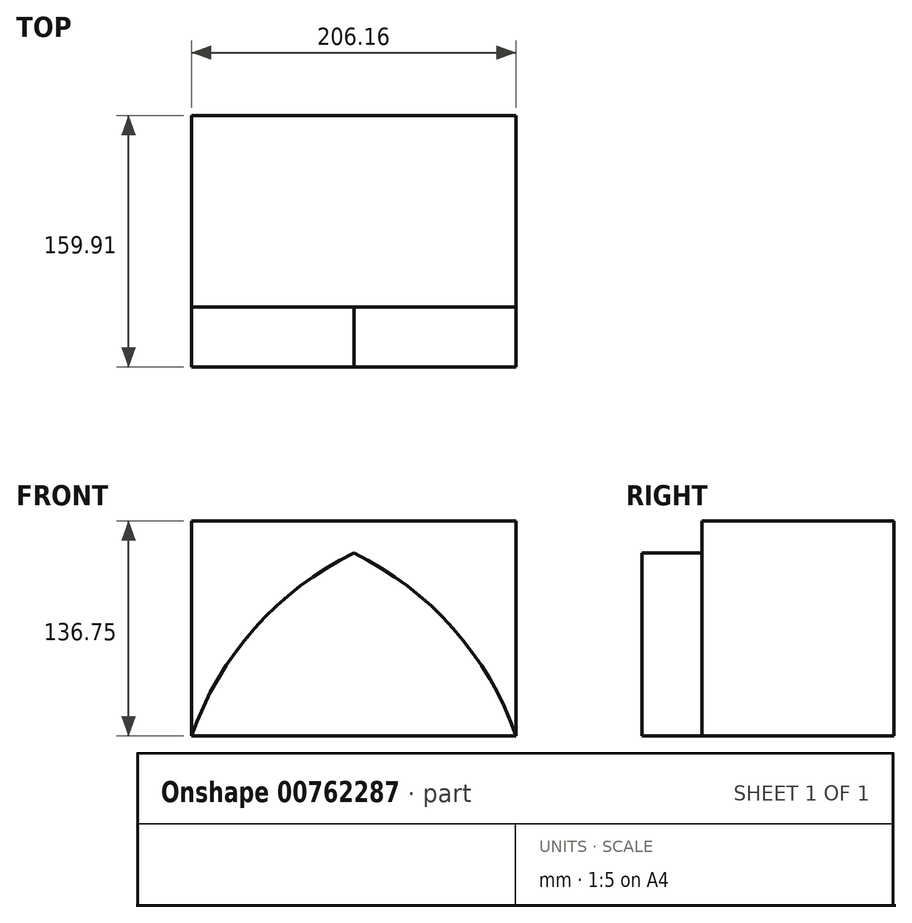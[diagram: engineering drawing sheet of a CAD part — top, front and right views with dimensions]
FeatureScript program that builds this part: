
annotation { "Feature Type Name" : "Feature", "Feature Type Description" : "" }
export const myFeature = defineFeature(function(context is Context, id is Id, definition is map)
    precondition{}
    {
        {
            var Q0;
            Q0=qCreatedBy(makeId("Front.planeOp"),FACE);
            var sketch = newSketch(context, id + "F0", { "sketchPlane" : qUnion([Q0])});
            skLineSegment(sketch, "E0.bottom", {"start": v(104.14, 68.47) * mm, "end": v(-102.02, 68.47) * mm});
            skLineSegment(sketch, "E0.top", {"start": v(104.14, -68.28) * mm, "end": v(-102.02, -68.28) * mm});
            skLineSegment(sketch, "E0.left", {"start": v(104.14, 68.47) * mm, "end": v(104.14, -68.28) * mm});
            skLineSegment(sketch, "E0.right", {"start": v(-102.02, 68.47) * mm, "end": v(-102.02, -68.28) * mm});
            skPoint(sketch, "E0.middle", {"position": v(1.06, 0.1) * mm});
            skSolve(sketch);
        }
        {
            var Q0;
            Q0 = qSketchRegion(id + "F0", true);
            var sketch = newSketch(context, id + "F1", { "sketchPlane" : qUnion([Q0])});
            skSolve(sketch);
        }
        {
            var Q0;
            Q0 = qSketchRegion(id + "F0", true);
            var sketch = newSketch(context, id + "F2", { "sketchPlane" : qUnion([Q0])});
            skSolve(sketch);
        }
        {
            var Q0;
            Q0=makeQuery(id+"F0.imprint","IMPRINT",FACE,{"disambiguationData":[TD([[makeQuery(id+"F0.imprint","IMPRINT",EDGE,{"derivedFrom":sQuery(id+"F0.wireOp",EDGE,"E0.bottom")}),1.0]])]});
            extrude(context, id + "F3", {"entities" : qUnion([Q0]), "depth" : 38.13 * mm, "offsetDistance" : 25.4 * mm});
        }
        {
            var Q0;
            Q0=makeQuery(id+"F3.opExtrude","CAP_FACE",FACE,{"disambiguationData":[OSD([sQuery(id+"F0.wireOp",EDGE,"E0.bottom"),sQuery(id+"F0.wireOp",EDGE,"E0.top"),sQuery(id+"F0.wireOp",EDGE,"E0.left"),sQuery(id+"F0.wireOp",EDGE,"E0.right")])],"isStart":false});
            var sketch = newSketch(context, id + "F4", { "sketchPlane" : qUnion([Q0])});
            skSolve(sketch);
        }
        {
            var Q0;
            Q0=makeQuery(id+"F4.imprint","IMPRINT",FACE,{"disambiguationData":[TD([[makeQuery(id+"F4.imprint","IMPRINT",EDGE,{"derivedFrom":makeQuery(id+"F3.opExtrude","CAP_EDGE",EDGE,{"disambiguationData":[OSD([sQuery(id+"F0.wireOp",EDGE,"E0.bottom")])],"isStart":false})}),1.0]])]});
            var sketch = newSketch(context, id + "F5", { "sketchPlane" : qUnion([Q0])});
            skCircle(sketch, "E1", {"center": v(0, 0) * mm, "radius": 27.59 * mm});
            skCircle(sketch, "E2", {"center": v(0, 0) * mm, "radius": 39.8 * mm});
            skSolve(sketch);
        }
        {
            var Q0;
            Q0=sQuery(id+"F5.wireOp",EDGE,"E2");
            extrude(context, id + "F6", {"bodyType" : ToolBodyType.SURFACE, "surfaceEntities" : qUnion([Q0]), "depth" : 25.4 * mm, "offsetDistance" : 25.4 * mm});
        }
        {
            var Q0;
            Q0=makeQuery(id+"F3.opExtrude","SWEPT_EDGE",EDGE,{"disambiguationData":[OSD([sQuery(id+"F0.wireOp",EDGE,"E0.bottom"),sQuery(id+"F0.wireOp",EDGE,"E0.left")])]});
            var Q1;
            Q1=makeQuery(id+"F3.opExtrude","SWEPT_EDGE",EDGE,{"disambiguationData":[OSD([sQuery(id+"F0.wireOp",EDGE,"E0.bottom"),sQuery(id+"F0.wireOp",EDGE,"E0.right")])]});
            fillet(context, id + "F7", {"entities" : qUnion([Q0, Q1]), "radius" : 203.2 * mm, "tangentPropagation" : true, "allowEdgeOverflow" : false});
        }
        {
            var Q0;
            Q0=makeQuery(id+"F1.imprint","IMPRINT",FACE,{"disambiguationData":[TD([[makeQuery(id+"F1.imprint","IMPRINT",EDGE,{"derivedFrom":makeQuery(id+"F0.imprint","IMPRINT",EDGE,{"derivedFrom":sQuery(id+"F0.wireOp",EDGE,"E0.bottom")})}),1.0]])]});
            var sketch = newSketch(context, id + "F8", { "sketchPlane" : qUnion([Q0])});
            skLineSegment(sketch, "E3.bottom", {"start": v(-47.78, -12.77) * mm, "end": v(69.72, -12.77) * mm});
            skLineSegment(sketch, "E3.top", {"start": v(-47.78, 6.05) * mm, "end": v(69.72, 6.05) * mm});
            skLineSegment(sketch, "E3.left", {"start": v(-47.78, -12.77) * mm, "end": v(-47.78, 6.05) * mm});
            skLineSegment(sketch, "E3.right", {"start": v(69.72, -12.77) * mm, "end": v(69.72, 6.05) * mm});
            skPoint(sketch, "E3.middle", {"position": v(10.97, -3.36) * mm});
            skLineSegment(sketch, "E4.bottom", {"start": v(-87.39, -40.87) * mm, "end": v(87.39, -40.87) * mm});
            skLineSegment(sketch, "E4.top", {"start": v(-87.39, -24.35) * mm, "end": v(87.39, -24.35) * mm});
            skLineSegment(sketch, "E4.left", {"start": v(-87.39, -40.87) * mm, "end": v(-87.39, -24.35) * mm});
            skLineSegment(sketch, "E4.right", {"start": v(87.39, -40.87) * mm, "end": v(87.39, -24.35) * mm});
            skPoint(sketch, "E4.middle", {"position": v(0, -32.6) * mm});
            skSolve(sketch);
        }
        {
            var Q0;
            Q0=makeQuery(id+"F8.imprint","IMPRINT",FACE,{"disambiguationData":[TD([[makeQuery(id+"F8.imprint","IMPRINT",EDGE,{"derivedFrom":sQuery(id+"F8.wireOp",EDGE,"E3.bottom")}),-1.0]])]});
            var Q1;
            Q1=makeQuery(id+"F2.imprint","IMPRINT",FACE,{"disambiguationData":[TD([[makeQuery(id+"F2.imprint","IMPRINT",EDGE,{"derivedFrom":makeQuery(id+"F0.imprint","IMPRINT",EDGE,{"derivedFrom":sQuery(id+"F0.wireOp",EDGE,"E0.bottom")})}),1.0]])]});
            extrude(context, id + "F9", {"entities" : qUnion([Q0, Q1]), "operationType" : NewBodyOperationType.ADD, "oppositeDirection" : true, "depth" : 121.78 * mm, "offsetDistance" : 25.4 * mm});
        }
    });
